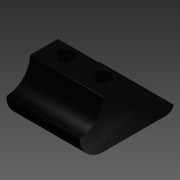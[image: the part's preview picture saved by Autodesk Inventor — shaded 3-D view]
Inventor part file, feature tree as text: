
AUTODESK INVENTOR PART (.ipt)
format: ipt  version: 2015 (Build 190159000, 159)  size: 155,648 bytes
history: native  units: mm
features: fillet x3, sketch x3, extrude x2, other x1, hole x1
ambient origin geometry x8: Origin, YZ Plane, XZ Plane, XY Plane, X Axis, Y Axis, Z Axis, Center Point
bodies: Body1 (feature_tree)
feature tree (10):
  other  "Bryła1"
  extrude  "Wyciągnięcie proste1"  Depth=28.0mm
  extrude  "Wyciągnięcie proste2"  Depth=36.0mm
  fillet  "Zaokrąglenie1"  Radius=18.0mm
  fillet  "Zaokrąglenie2"  Radius=18.0mm
  fillet  "Zaokrąglenie3"  Radius=32.0mm
  hole  "Otwór1"  [1 undecoded]
  sketch  "Szkic1"
  sketch  "Szkic3"
  sketch  "Szkic4"
note: 1 required parameter value undecoded (feature->parameter linkage not recoverable at this tier; creation-order binding heuristic only, values carry confidence <= 0.55)
